# Revit family: PRD_FrankeWS_SnkMnlWtrSpplSts_SIRIUSBucketGrating_SIRX512
name_source: partatom
category: Furniture
revit_build: Autodesk Revit 2018 (Build: 20190510_1515(x64)
units: mm (PartAtom-declared; Revit-internal decimal feet)

## family parameters
Cut with Voids When Loaded = No
Host = Face
OmniClass Number = 23.45.05.14.99
OmniClass Title = Other Sanitary Washing Plumbing Fixtures
Room Calculation Point = No
Shared = No

## types (1)
- SIRX512
    AssetType = Fixed
    BIMObjectName = PRD_AR_SinkManualWaterSupplySets_SIRIUSBucketGrating_SIRX512
    Category = Pr_40_20_87_82, Sink manual water supply sets
    Default Elevation = 1000 mm  [stored 3.28084 ft]
    Description = Bucket grating made of nickel-chromium steel for wall mounting above disposal sink made of MIRANIT, hinged, with tilt protection, fastening material included.
    DurationUnit = year
    Features = nickel-chromium steel for wall mounting above disposal sink
    Finish = Nickel-chromed
    GrossWeight = 2.28 kg
    IfcExportAs = IfcSanitaryTerminalType
    IfcExportType = USERDEFINED
    IntegralAccessories = fastening material incl.
    MainColor = stainless steel
    MainMaterial = PRD_AR_Steel_NickelChromed
    Manufacturer = KWC Group AG
    ManufacturerName = KWC Group AG
    ManufacturerURL = www.kwc.com
    Material = Steel
    Model = SIRX512
    ModelNumber = 2000101201
    ModelReference = SIRX512
    NBSDescription = Water supply fittings for sinks
    NBSReference = 45-35-70/345
    Name = SIRIUS Bucket grating SIRX512
    NetWeight = 2.17 kg
    NominalDepth = 362 mm  [stored 1.18766 ft]
    NominalHeight = 118 mm
    NominalLength = 0 mm  [stored 0 ft]
    NominalWidth = 360 mm  [stored 1.1811 ft]
    ProductCode = 207.0611.708
    ProductInformation = https://pim.kwc.com
    Quantity = 1
    QuantityUom = Piece
    Size = 360 x 118 x 362 mm (W x H x D)
    Status = New
    TailorMade = No
    URL = www.kwc.com
    Uniclass2015Code = Pr_40_20_87_82
    Uniclass2015Title = Sink manual water supply sets
    Uniclass2015Version = Products v1.17
    Version = 1
    WarrantyDurationUnit = year

note: [stored X ft] marks values corroborated as IEEE doubles in the binary element streams (Revit-internal decimal feet)

## geometry (parser evidence)
native form markers: Sweep x2
no freeform markers — native parametric forms only
